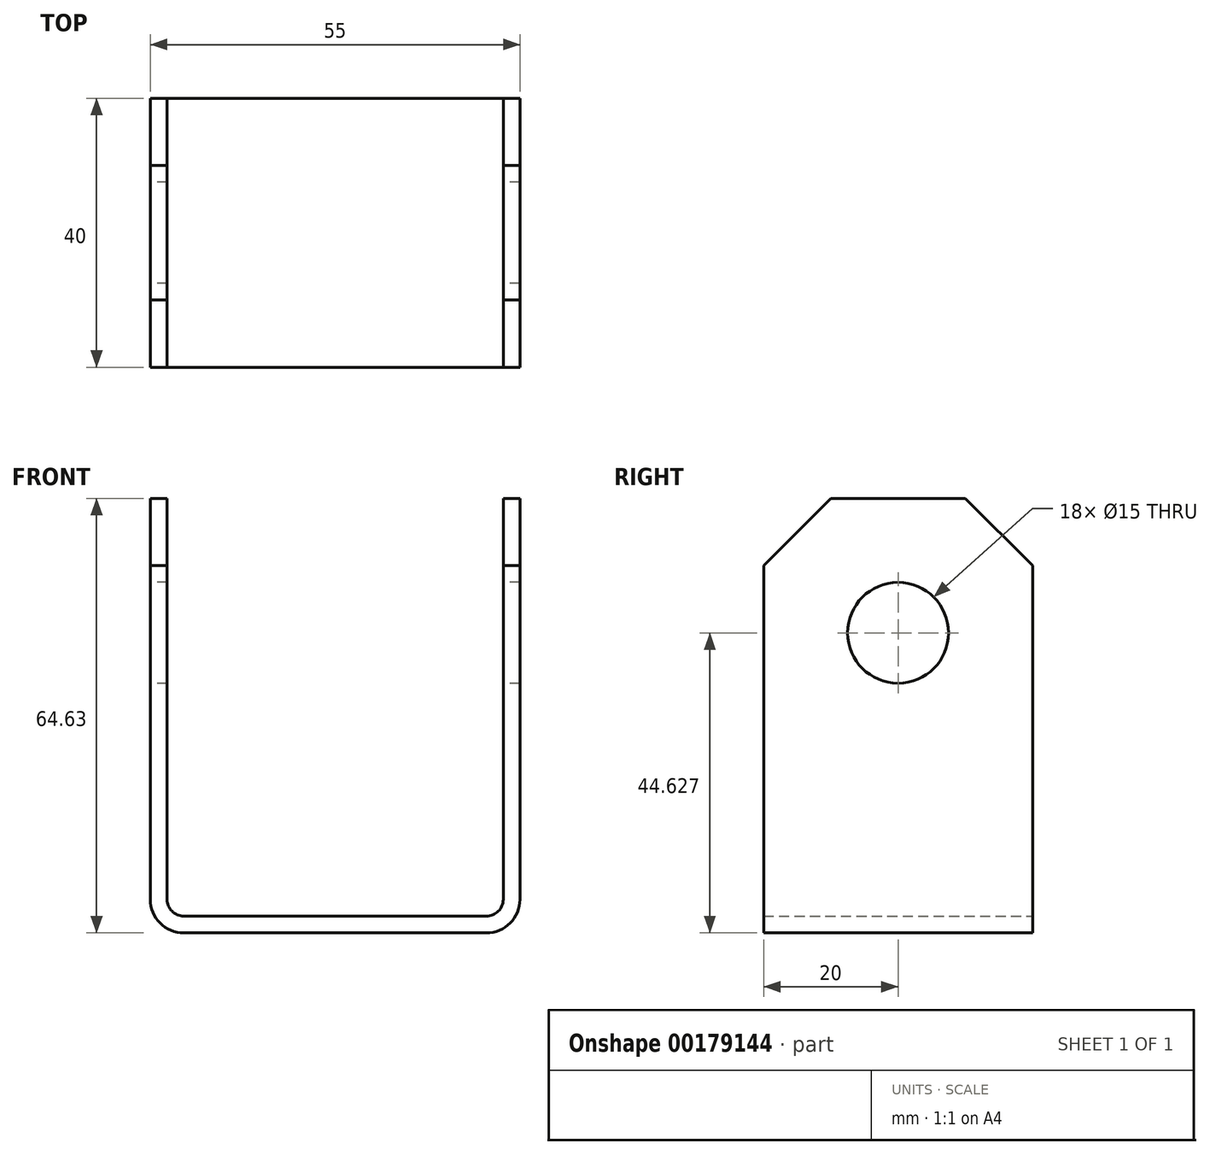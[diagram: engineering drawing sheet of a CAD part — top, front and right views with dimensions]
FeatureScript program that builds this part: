
annotation { "Feature Type Name" : "Feature", "Feature Type Description" : "" }
export const myFeature = defineFeature(function(context is Context, id is Id, definition is map)
    precondition{}
    {
        {
            var Q0;
            Q0=qCreatedBy(makeId("Front.planeOp"),FACE);
            var sketch = newSketch(context, id + "F0", { "sketchPlane" : qUnion([Q0])});
            skLineSegment(sketch, "E0.bottom", {"start": v(-27.5, 0) * mm, "end": v(27.5, 0) * mm});
            skLineSegment(sketch, "E0.top", {"start": v(-27.5, 64.63) * mm, "end": v(27.5, 64.63) * mm});
            skLineSegment(sketch, "E0.left", {"start": v(-27.5, 0) * mm, "end": v(-27.5, 64.63) * mm});
            skLineSegment(sketch, "E0.right", {"start": v(27.5, 0) * mm, "end": v(27.5, 64.63) * mm});
            skSolve(sketch);
        }
        {
            var Q0;
            Q0 = qSketchRegion(id + "F0", true);
            extrude(context, id + "F1", {"entities" : qUnion([Q0]), "depth" : 20 * mm, "hasSecondDirection" : true, "secondDirectionOppositeDirection" : true, "secondDirectionDepth" : 20 * mm});
        }
        {
            var Q0;
            Q0=makeQuery(id+"F1.opExtrude","CAP_EDGE",EDGE,{"disambiguationData":[OSD([sQuery(id+"F0.wireOp",EDGE,"E0.top")])],"isStart":false});
            var Q1;
            Q1=makeQuery(id+"F1.opExtrude","CAP_EDGE",EDGE,{"disambiguationData":[OSD([sQuery(id+"F0.wireOp",EDGE,"E0.top")])],"isStart":true});
            chamfer(context, id + "F2", {"entities" : qUnion([Q0, Q1]), "width" : 10 * mm, "tangentPropagation" : true});
        }
        {
            var Q0;
            Q0=makeQuery(id+"F1.opExtrude","SWEPT_EDGE",EDGE,{"disambiguationData":[OSD([sQuery(id+"F0.wireOp",EDGE,"E0.bottom"),sQuery(id+"F0.wireOp",EDGE,"E0.left")])]});
            var Q1;
            Q1=makeQuery(id+"F1.opExtrude","SWEPT_EDGE",EDGE,{"disambiguationData":[OSD([sQuery(id+"F0.wireOp",EDGE,"E0.bottom"),sQuery(id+"F0.wireOp",EDGE,"E0.right")])]});
            fillet(context, id + "F3", {"entities" : qUnion([Q0, Q1]), "radius" : 5 * mm, "tangentPropagation" : true, "allowEdgeOverflow" : false});
        }
        {
            var Q0;
            Q0=makeQuery(id+"F1.opExtrude","CAP_FACE",FACE,{"disambiguationData":[OSD([sQuery(id+"F0.wireOp",EDGE,"E0.bottom"),sQuery(id+"F0.wireOp",EDGE,"E0.top"),sQuery(id+"F0.wireOp",EDGE,"E0.left"),sQuery(id+"F0.wireOp",EDGE,"E0.right")])],"isStart":false});
            var Q1;
            {var subQ0=sQuery(id+"F0.wireOp",EDGE,"E0.top");Q1=makeQuery(id+"F2.opChamfer","BLEND_FACE",FACE,{"disambiguationData":[OSD([subQ0]),TDD([makeQuery(id+"F1.opExtrude","CAP_EDGE",EDGE,{"disambiguationData":[OSD([subQ0])],"isStart":false})])]});}
            var Q2;
            Q2=makeQuery(id+"F1.opExtrude","SWEPT_FACE",FACE,{"disambiguationData":[OSD([sQuery(id+"F0.wireOp",EDGE,"E0.top")])]});
            var Q3;
            {var subQ0=sQuery(id+"F0.wireOp",EDGE,"E0.top");Q3=makeQuery(id+"F2.opChamfer","BLEND_FACE",FACE,{"disambiguationData":[OSD([subQ0]),TDD([makeQuery(id+"F1.opExtrude","CAP_EDGE",EDGE,{"disambiguationData":[OSD([subQ0])],"isStart":true})])]});}
            var Q4;
            Q4=makeQuery(id+"F1.opExtrude","CAP_FACE",FACE,{"disambiguationData":[OSD([sQuery(id+"F0.wireOp",EDGE,"E0.bottom"),sQuery(id+"F0.wireOp",EDGE,"E0.top"),sQuery(id+"F0.wireOp",EDGE,"E0.left"),sQuery(id+"F0.wireOp",EDGE,"E0.right")])],"isStart":true});
            shell(context, id + "F4", {"entities" : qUnion([Q0, Q1, Q2, Q3, Q4]), "thickness" : 2.5 * mm});
        }
        {
            var Q0;
            Q0=makeQuery(id+"F1.opExtrude","SWEPT_FACE",FACE,{"disambiguationData":[OSD([sQuery(id+"F0.wireOp",EDGE,"E0.left")])]});
            var sketch = newSketch(context, id + "F5", { "sketchPlane" : qUnion([Q0])});
            skPoint(sketch, "E1", {"position": v(0, 44.63) * mm});
            skSolve(sketch);
        }
        {
            var Q0;
            Q0=sQuery(id+"F5.wireOp",VERTEX,"E1");
            var Q1;
            Q1=makeQuery(id+"F1.opExtrude","SWEPT_BODY",BODY,{"disambiguationData":[OSD([sQuery(id+"F0.wireOp",EDGE,"E0.bottom"),sQuery(id+"F0.wireOp",EDGE,"E0.top"),sQuery(id+"F0.wireOp",EDGE,"E0.left"),sQuery(id+"F0.wireOp",EDGE,"E0.right")])]});
            hole(context, id + "F6", {"style" : HoleStyle.SIMPLE, "endStyle" : HoleEndStyle.THROUGH, "holeDiameter" : 15 * mm, "locations" : qUnion([Q0]), "scope" : qUnion([Q1]), "isTappedThrough" : true});
        }
    });
